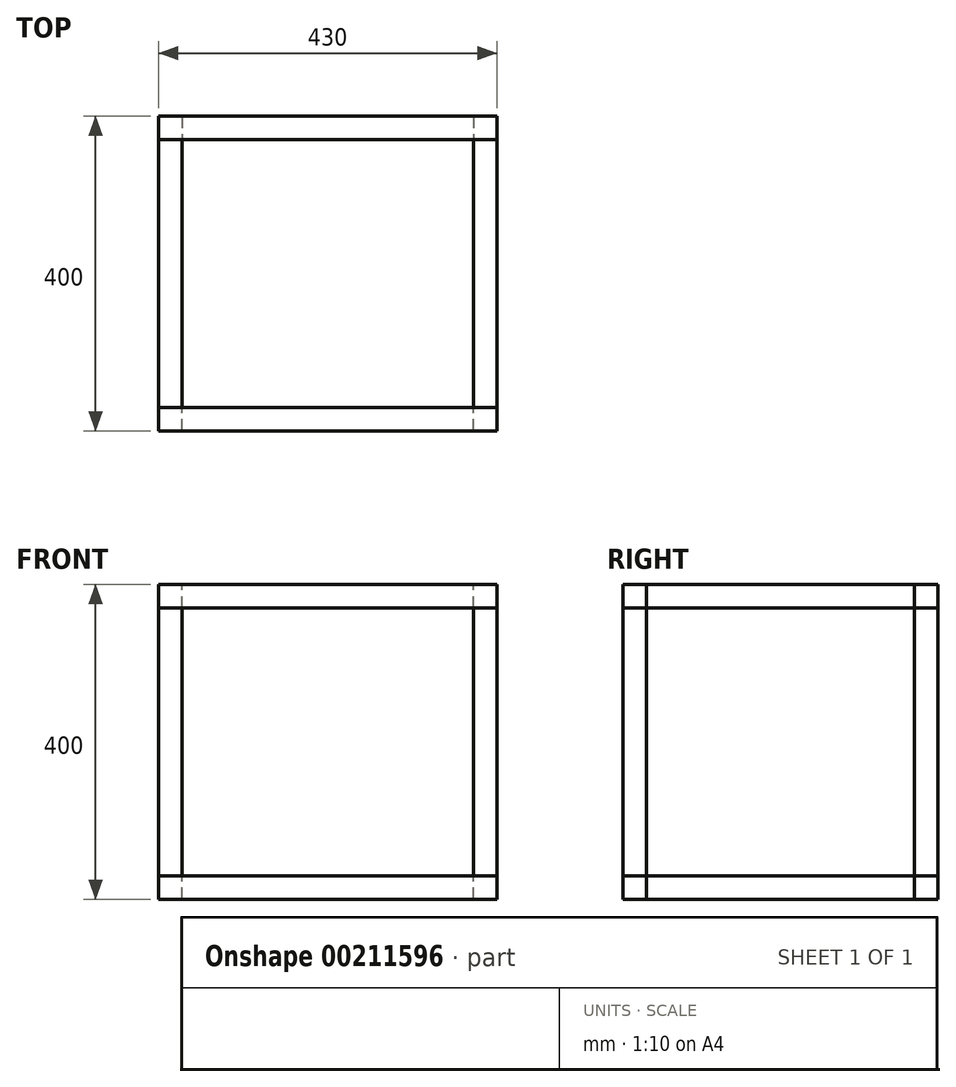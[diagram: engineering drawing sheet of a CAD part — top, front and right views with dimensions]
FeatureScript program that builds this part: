
annotation { "Feature Type Name" : "Feature", "Feature Type Description" : "" }
export const myFeature = defineFeature(function(context is Context, id is Id, definition is map)
    precondition{}
    {
        {
            var Q0;
            Q0=qCreatedBy(makeId("Front.planeOp"),FACE);
            var sketch = newSketch(context, id + "F0", { "sketchPlane" : qUnion([Q0])});
            skLineSegment(sketch, "E0.bottom", {"start": v(0, 0) * mm, "end": v(30, 0) * mm});
            skLineSegment(sketch, "E0.top", {"start": v(0, 30) * mm, "end": v(30, 30) * mm});
            skLineSegment(sketch, "E0.left", {"start": v(0, 0) * mm, "end": v(0, 30) * mm});
            skLineSegment(sketch, "E0.right", {"start": v(30, 0) * mm, "end": v(30, 30) * mm});
            skLineSegment(sketch, "E1.0.1.0", {"start": v(0, 370) * mm, "end": v(30, 370) * mm});
            skLineSegment(sketch, "E1.0.1.1", {"start": v(0, 370) * mm, "end": v(0, 400) * mm});
            skLineSegment(sketch, "E1.0.1.2", {"start": v(0, 400) * mm, "end": v(30, 400) * mm});
            skLineSegment(sketch, "E1.0.1.3", {"start": v(30, 370) * mm, "end": v(30, 400) * mm});
            skLineSegment(sketch, "E1.1.0.0", {"start": v(400, 0) * mm, "end": v(430, 0) * mm});
            skLineSegment(sketch, "E1.1.0.1", {"start": v(400, 0) * mm, "end": v(400, 30) * mm});
            skLineSegment(sketch, "E1.1.0.2", {"start": v(400, 30) * mm, "end": v(430, 30) * mm});
            skLineSegment(sketch, "E1.1.0.3", {"start": v(430, 0) * mm, "end": v(430, 30) * mm});
            skLineSegment(sketch, "E1.1.1.0", {"start": v(400, 370) * mm, "end": v(430, 370) * mm});
            skLineSegment(sketch, "E1.1.1.1", {"start": v(400, 370) * mm, "end": v(400, 400) * mm});
            skLineSegment(sketch, "E1.1.1.2", {"start": v(400, 400) * mm, "end": v(430, 400) * mm});
            skLineSegment(sketch, "E1.1.1.3", {"start": v(430, 370) * mm, "end": v(430, 400) * mm});
            skLineSegment(sketch, "E1.direction1", {"start": v(0, 0) * mm, "end": v(400, 0) * mm, "construction": true});
            skLineSegment(sketch, "E1.direction2", {"start": v(0, 0) * mm, "end": v(0, 370) * mm, "construction": true});
            skSolve(sketch);
        }
        {
            var Q0;
            Q0=qCreatedBy(makeId("Top.planeOp"),FACE);
            var sketch = newSketch(context, id + "F1", { "sketchPlane" : qUnion([Q0])});
            skLineSegment(sketch, "E2.bottom", {"start": v(30, 0) * mm, "end": v(430, 0) * mm, "construction": true});
            skLineSegment(sketch, "E2.top", {"start": v(30, 400) * mm, "end": v(430, 400) * mm, "construction": true});
            skLineSegment(sketch, "E2.left", {"start": v(30, 0) * mm, "end": v(30, 400) * mm, "construction": true});
            skLineSegment(sketch, "E2.right", {"start": v(430, 0) * mm, "end": v(430, 400) * mm, "construction": true});
            skLineSegment(sketch, "E3.bottom", {"start": v(30, 0) * mm, "end": v(60, 0) * mm});
            skLineSegment(sketch, "E3.top", {"start": v(30, 30) * mm, "end": v(60, 30) * mm});
            skLineSegment(sketch, "E3.left", {"start": v(30, 0) * mm, "end": v(30, 30) * mm});
            skLineSegment(sketch, "E3.right", {"start": v(60, 0) * mm, "end": v(60, 30) * mm});
            skLineSegment(sketch, "E4.bottom", {"start": v(30, 400) * mm, "end": v(60, 400) * mm});
            skLineSegment(sketch, "E4.top", {"start": v(30, 370) * mm, "end": v(60, 370) * mm});
            skLineSegment(sketch, "E4.left", {"start": v(30, 400) * mm, "end": v(30, 370) * mm});
            skLineSegment(sketch, "E4.right", {"start": v(60, 400) * mm, "end": v(60, 370) * mm});
            skLineSegment(sketch, "E5.bottom", {"start": v(430, 400) * mm, "end": v(400, 400) * mm});
            skLineSegment(sketch, "E5.top", {"start": v(430, 370) * mm, "end": v(400, 370) * mm});
            skLineSegment(sketch, "E5.left", {"start": v(430, 400) * mm, "end": v(430, 370) * mm});
            skLineSegment(sketch, "E5.right", {"start": v(400, 400) * mm, "end": v(400, 370) * mm});
            skLineSegment(sketch, "E6.bottom", {"start": v(430, 0) * mm, "end": v(400, 0) * mm});
            skLineSegment(sketch, "E6.top", {"start": v(430, 30) * mm, "end": v(400, 30) * mm});
            skLineSegment(sketch, "E6.left", {"start": v(430, 0) * mm, "end": v(430, 30) * mm});
            skLineSegment(sketch, "E6.right", {"start": v(400, 0) * mm, "end": v(400, 30) * mm});
            skLineSegment(sketch, "E7.bottom", {"start": v(30, 370) * mm, "end": v(0, 370) * mm});
            skLineSegment(sketch, "E7.top", {"start": v(30, 400) * mm, "end": v(0, 400) * mm});
            skLineSegment(sketch, "E7.left", {"start": v(30, 370) * mm, "end": v(30, 400) * mm});
            skLineSegment(sketch, "E7.right", {"start": v(0, 370) * mm, "end": v(0, 400) * mm});
            skPoint(sketch, "E8.oppositeSnap0", {"position": v(45, 30) * mm});
            skLineSegment(sketch, "E8.bottom", {"start": v(30, 0) * mm, "end": v(0, 0) * mm});
            skLineSegment(sketch, "E8.top", {"start": v(30, 30) * mm, "end": v(0, 30) * mm});
            skLineSegment(sketch, "E8.right", {"start": v(0, 0) * mm, "end": v(0, 30) * mm});
            skSolve(sketch);
        }
        {
            var Q0;
            Q0=qCreatedBy(makeId("Right.planeOp"),FACE);
            var sketch = newSketch(context, id + "F2", { "sketchPlane" : qUnion([Q0])});
            skLineSegment(sketch, "E9.bottom", {"start": v(0, 0) * mm, "end": v(400, 0) * mm, "construction": true});
            skLineSegment(sketch, "E9.top", {"start": v(0, 400) * mm, "end": v(400, 400) * mm, "construction": true});
            skLineSegment(sketch, "E9.left", {"start": v(0, 0) * mm, "end": v(0, 400) * mm, "construction": true});
            skLineSegment(sketch, "E9.right", {"start": v(400, 0) * mm, "end": v(400, 400) * mm, "construction": true});
            skLineSegment(sketch, "E10.bottom", {"start": v(0, 400) * mm, "end": v(30, 400) * mm});
            skLineSegment(sketch, "E10.top", {"start": v(0, 370) * mm, "end": v(30, 370) * mm});
            skLineSegment(sketch, "E10.left", {"start": v(0, 400) * mm, "end": v(0, 370) * mm});
            skLineSegment(sketch, "E10.right", {"start": v(30, 400) * mm, "end": v(30, 370) * mm});
            skLineSegment(sketch, "E11.bottom", {"start": v(400, 400) * mm, "end": v(370, 400) * mm});
            skLineSegment(sketch, "E11.top", {"start": v(400, 370) * mm, "end": v(370, 370) * mm});
            skLineSegment(sketch, "E11.left", {"start": v(400, 400) * mm, "end": v(400, 370) * mm});
            skLineSegment(sketch, "E11.right", {"start": v(370, 400) * mm, "end": v(370, 370) * mm});
            skLineSegment(sketch, "E12.bottom", {"start": v(0, 0) * mm, "end": v(30, 0) * mm});
            skLineSegment(sketch, "E12.top", {"start": v(0, 30) * mm, "end": v(30, 30) * mm});
            skLineSegment(sketch, "E12.left", {"start": v(0, 0) * mm, "end": v(0, 30) * mm});
            skLineSegment(sketch, "E12.right", {"start": v(30, 0) * mm, "end": v(30, 30) * mm});
            skLineSegment(sketch, "E13.bottom", {"start": v(370, 30) * mm, "end": v(400, 30) * mm});
            skLineSegment(sketch, "E13.top", {"start": v(370, 0) * mm, "end": v(400, 0) * mm});
            skLineSegment(sketch, "E13.left", {"start": v(370, 30) * mm, "end": v(370, 0) * mm});
            skLineSegment(sketch, "E13.right", {"start": v(400, 30) * mm, "end": v(400, 0) * mm});
            skSolve(sketch);
        }
        {
            var Q0;
            Q0=makeQuery(id+"F0.imprint","IMPRINT",FACE,{"disambiguationData":[TD([[makeQuery(id+"F0.imprint","IMPRINT",EDGE,{"derivedFrom":sQuery(id+"F0.wireOp",EDGE,"E1.0.1.0")}),1.0]])]});
            var Q1;
            Q1=makeQuery(id+"F0.imprint","IMPRINT",FACE,{"disambiguationData":[TD([[makeQuery(id+"F0.imprint","IMPRINT",EDGE,{"derivedFrom":sQuery(id+"F0.wireOp",EDGE,"E0.bottom")}),1.0]])]});
            var Q2;
            Q2=makeQuery(id+"F0.imprint","IMPRINT",FACE,{"disambiguationData":[TD([[makeQuery(id+"F0.imprint","IMPRINT",EDGE,{"derivedFrom":sQuery(id+"F0.wireOp",EDGE,"E1.1.0.0")}),1.0]])]});
            var Q3;
            Q3=makeQuery(id+"F0.imprint","IMPRINT",FACE,{"disambiguationData":[TD([[makeQuery(id+"F0.imprint","IMPRINT",EDGE,{"derivedFrom":sQuery(id+"F0.wireOp",EDGE,"E1.1.1.0")}),1.0]])]});
            var Q4;
            Q4=sQuery(id+"F2.wireOp",VERTEX,"E11.right.start");
            var Q5;
            Q5=sQuery(id+"F2.wireOp",VERTEX,"E10.top.end");
            extrude(context, id + "F3", {"entities" : qUnion([Q0, Q1, Q2, Q3]), "endBound" : BoundingType.UP_TO_VERTEX, "oppositeDirection" : true, "endBoundEntityVertex" : qUnion([Q4]), "depth" : 277 * mm, "hasSecondDirection" : true, "secondDirectionBound" : BoundingType.UP_TO_VERTEX, "secondDirectionOppositeDirection" : true, "secondDirectionBoundEntityVertex" : qUnion([Q5]), "secondDirectionDepth" : 25 * mm});
        }
        {
            var Q0;
            Q0=makeQuery(id+"F2.imprint","IMPRINT",FACE,{"disambiguationData":[TD([[makeQuery(id+"F2.imprint","IMPRINT",EDGE,{"derivedFrom":sQuery(id+"F2.wireOp",EDGE,"E11.bottom")}),1.0]])]});
            var Q1;
            Q1=makeQuery(id+"F2.imprint","IMPRINT",FACE,{"disambiguationData":[TD([[makeQuery(id+"F2.imprint","IMPRINT",EDGE,{"derivedFrom":sQuery(id+"F2.wireOp",EDGE,"E13.bottom")}),-1.0]])]});
            var Q2;
            Q2=makeQuery(id+"F2.imprint","IMPRINT",FACE,{"disambiguationData":[TD([[makeQuery(id+"F2.imprint","IMPRINT",EDGE,{"derivedFrom":sQuery(id+"F2.wireOp",EDGE,"E12.bottom")}),1.0]])]});
            var Q3;
            Q3=makeQuery(id+"F2.imprint","IMPRINT",FACE,{"disambiguationData":[TD([[makeQuery(id+"F2.imprint","IMPRINT",EDGE,{"derivedFrom":sQuery(id+"F2.wireOp",EDGE,"E10.bottom")}),-1.0]])]});
            var Q4;
            Q4=sQuery(id+"F0.wireOp",VERTEX,"E1.1.1.3.end");
            extrude(context, id + "F4", {"entities" : qUnion([Q0, Q1, Q2, Q3]), "endBound" : BoundingType.UP_TO_VERTEX, "endBoundEntityVertex" : qUnion([Q4]), "depth" : 25 * mm});
        }
        {
            var Q0;
            Q0=makeQuery(id+"F1.imprint","IMPRINT",FACE,{"disambiguationData":[TD([[makeQuery(id+"F1.imprint","IMPRINT",EDGE,{"derivedFrom":sQuery(id+"F1.wireOp",EDGE,"E8.bottom")}),-1.0]])]});
            var Q1;
            Q1=makeQuery(id+"F1.imprint","IMPRINT",FACE,{"disambiguationData":[TD([[makeQuery(id+"F1.imprint","IMPRINT",EDGE,{"derivedFrom":sQuery(id+"F1.wireOp",EDGE,"E6.bottom")}),-1.0]])]});
            var Q2;
            Q2=makeQuery(id+"F1.imprint","IMPRINT",FACE,{"disambiguationData":[TD([[makeQuery(id+"F1.imprint","IMPRINT",EDGE,{"derivedFrom":sQuery(id+"F1.wireOp",EDGE,"E5.bottom")}),1.0]])]});
            var Q3;
            Q3=makeQuery(id+"F1.imprint","IMPRINT",FACE,{"disambiguationData":[TD([[makeQuery(id+"F1.imprint","IMPRINT",EDGE,{"derivedFrom":sQuery(id+"F1.wireOp",EDGE,"E7.bottom")}),-1.0]])]});
            var Q4;
            Q4=sQuery(id+"F2.wireOp",VERTEX,"E10.top.start");
            var Q5;
            Q5=sQuery(id+"F0.wireOp",VERTEX,"E0.right.end");
            extrude(context, id + "F5", {"entities" : qUnion([Q0, Q1, Q2, Q3]), "endBound" : BoundingType.UP_TO_VERTEX, "endBoundEntityVertex" : qUnion([Q4]), "depth" : 25 * mm, "hasSecondDirection" : true, "secondDirectionBound" : BoundingType.UP_TO_VERTEX, "secondDirectionOppositeDirection" : false, "secondDirectionBoundEntityVertex" : qUnion([Q5]), "secondDirectionDepth" : 25 * mm});
        }
    });
